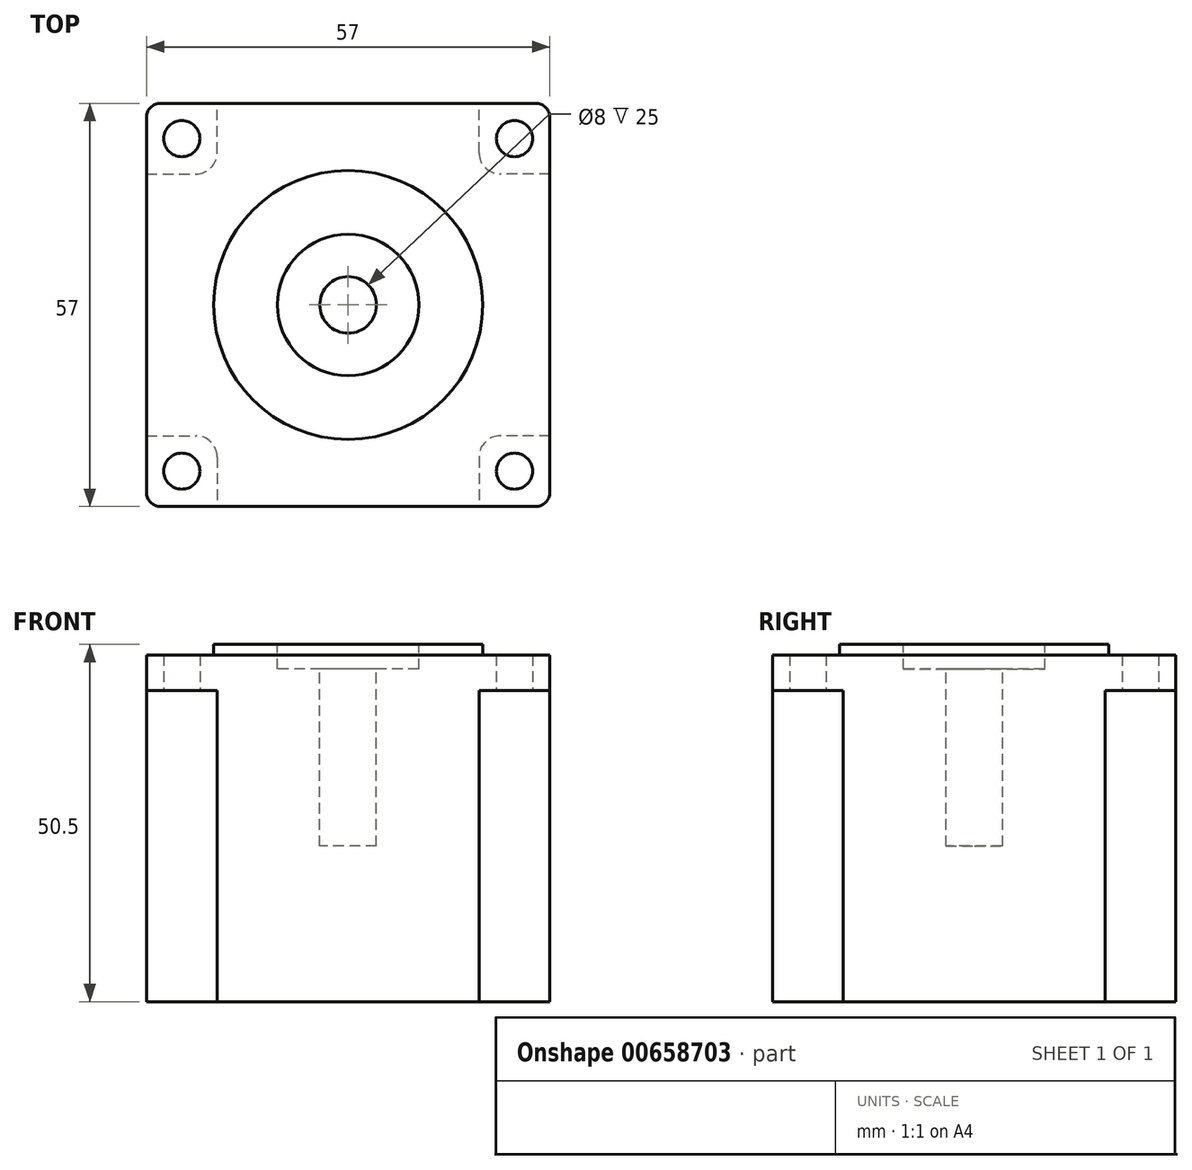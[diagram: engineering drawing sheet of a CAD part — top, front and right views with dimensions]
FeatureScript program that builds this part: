
annotation { "Feature Type Name" : "Feature", "Feature Type Description" : "" }
export const myFeature = defineFeature(function(context is Context, id is Id, definition is map)
    precondition{}
    {
        {
            var Q0;
            Q0=qCreatedBy(makeId("Top.planeOp"),FACE);
            var sketch = newSketch(context, id + "F0", { "sketchPlane" : qUnion([Q0])});
            skLineSegment(sketch, "E0.bottom", {"start": v(-28.5, 28.5) * mm, "end": v(28.5, 28.5) * mm});
            skLineSegment(sketch, "E0.top", {"start": v(-28.5, -28.5) * mm, "end": v(28.5, -28.5) * mm});
            skLineSegment(sketch, "E0.left", {"start": v(-28.5, 28.5) * mm, "end": v(-28.5, -28.5) * mm});
            skLineSegment(sketch, "E0.right", {"start": v(28.5, 28.5) * mm, "end": v(28.5, -28.5) * mm});
            skSolve(sketch);
        }
        {
            var Q0;
            Q0=makeQuery(id+"F0.imprint","IMPRINT",FACE,{"disambiguationData":[TD([[makeQuery(id+"F0.imprint","IMPRINT",EDGE,{"derivedFrom":sQuery(id+"F0.wireOp",EDGE,"E0.bottom")}),-1.0]])]});
            extrude(context, id + "F1", {"entities" : qUnion([Q0]), "depth" : 49 * mm});
        }
        {
            var Q0;
            Q0=makeQuery(id+"F1.opExtrude","SWEPT_EDGE",EDGE,{"disambiguationData":[OSD([sQuery(id+"F0.wireOp",EDGE,"E0.top"),sQuery(id+"F0.wireOp",EDGE,"E0.left")])]});
            var Q1;
            Q1=makeQuery(id+"F1.opExtrude","SWEPT_EDGE",EDGE,{"disambiguationData":[OSD([sQuery(id+"F0.wireOp",EDGE,"E0.top"),sQuery(id+"F0.wireOp",EDGE,"E0.right")])]});
            var Q2;
            Q2=makeQuery(id+"F1.opExtrude","SWEPT_EDGE",EDGE,{"disambiguationData":[OSD([sQuery(id+"F0.wireOp",EDGE,"E0.bottom"),sQuery(id+"F0.wireOp",EDGE,"E0.right")])]});
            var Q3;
            Q3=makeQuery(id+"F1.opExtrude","SWEPT_EDGE",EDGE,{"disambiguationData":[OSD([sQuery(id+"F0.wireOp",EDGE,"E0.bottom"),sQuery(id+"F0.wireOp",EDGE,"E0.left")])]});
            fillet(context, id + "F2", {"entities" : qUnion([Q0, Q1, Q2, Q3]), "radius" : 2 * mm, "tangentPropagation" : true, "allowEdgeOverflow" : false});
        }
        {
            var Q0;
            Q0=makeQuery(id+"F1.opExtrude","CAP_FACE",FACE,{"disambiguationData":[OSD([sQuery(id+"F0.wireOp",EDGE,"E0.bottom"),sQuery(id+"F0.wireOp",EDGE,"E0.top"),sQuery(id+"F0.wireOp",EDGE,"E0.left"),sQuery(id+"F0.wireOp",EDGE,"E0.right")])],"isStart":true});
            var sketch = newSketch(context, id + "F3", { "sketchPlane" : qUnion([Q0])});
            skCircle(sketch, "E1", {"center": v(-23.5, 23.5) * mm, "radius": 2.55 * mm});
            skCircle(sketch, "E2", {"center": v(-23.5, -23.5) * mm, "radius": 2.55 * mm});
            skCircle(sketch, "E3", {"center": v(23.5, -23.5) * mm, "radius": 2.55 * mm});
            skCircle(sketch, "E4", {"center": v(23.5, 23.5) * mm, "radius": 2.55 * mm});
            skSolve(sketch);
        }
        {
            var Q0;
            Q0=makeQuery(id+"F3.imprint","IMPRINT",FACE,{"disambiguationData":[TD([[makeQuery(id+"F3.imprint","IMPRINT",EDGE,{"derivedFrom":sQuery(id+"F3.wireOp",EDGE,"E2")}),1.0]])]});
            var Q1;
            Q1=makeQuery(id+"F3.imprint","IMPRINT",FACE,{"disambiguationData":[TD([[makeQuery(id+"F3.imprint","IMPRINT",EDGE,{"derivedFrom":sQuery(id+"F3.wireOp",EDGE,"E1")}),1.0]])]});
            var Q2;
            Q2=makeQuery(id+"F3.imprint","IMPRINT",FACE,{"disambiguationData":[TD([[makeQuery(id+"F3.imprint","IMPRINT",EDGE,{"derivedFrom":sQuery(id+"F3.wireOp",EDGE,"E4")}),1.0]])]});
            var Q3;
            Q3=makeQuery(id+"F3.imprint","IMPRINT",FACE,{"disambiguationData":[TD([[makeQuery(id+"F3.imprint","IMPRINT",EDGE,{"derivedFrom":sQuery(id+"F3.wireOp",EDGE,"E3")}),1.0]])]});
            extrude(context, id + "F4", {"entities" : qUnion([Q0, Q1, Q2, Q3]), "operationType" : NewBodyOperationType.REMOVE, "endBound" : BoundingType.THROUGH_ALL, "oppositeDirection" : true, "depth" : 25 * mm});
        }
        {
            var Q0;
            Q0=makeQuery(id+"F1.opExtrude","CAP_FACE",FACE,{"disambiguationData":[OSD([sQuery(id+"F0.wireOp",EDGE,"E0.bottom"),sQuery(id+"F0.wireOp",EDGE,"E0.top"),sQuery(id+"F0.wireOp",EDGE,"E0.left"),sQuery(id+"F0.wireOp",EDGE,"E0.right")])],"isStart":true});
            var sketch = newSketch(context, id + "F5", { "sketchPlane" : qUnion([Q0])});
            skLineSegment(sketch, "E5.rect.bottom", {"start": v(28.5, 18.5) * mm, "end": v(18.5, 18.5) * mm});
            skLineSegment(sketch, "E5.rect.top", {"start": v(28.5, 28.5) * mm, "end": v(18.5, 28.5) * mm});
            skLineSegment(sketch, "E5.rect.left", {"start": v(28.5, 18.5) * mm, "end": v(28.5, 28.5) * mm});
            skLineSegment(sketch, "E5.rect.right", {"start": v(18.5, 18.5) * mm, "end": v(18.5, 28.5) * mm});
            skPoint(sketch, "E5.rect.middle", {"position": v(23.5, 23.5) * mm});
            skLineSegment(sketch, "E6.rect.bottom", {"start": v(28.5, -18.5) * mm, "end": v(18.5, -18.5) * mm});
            skLineSegment(sketch, "E6.rect.top", {"start": v(28.5, -28.5) * mm, "end": v(18.5, -28.5) * mm});
            skLineSegment(sketch, "E6.rect.left", {"start": v(28.5, -18.5) * mm, "end": v(28.5, -28.5) * mm});
            skLineSegment(sketch, "E6.rect.right", {"start": v(18.5, -18.5) * mm, "end": v(18.5, -28.5) * mm});
            skPoint(sketch, "E6.rect.middle", {"position": v(23.5, -23.5) * mm});
            skLineSegment(sketch, "E7.rect.bottom", {"start": v(-28.5, -18.5) * mm, "end": v(-18.5, -18.5) * mm});
            skLineSegment(sketch, "E7.rect.top", {"start": v(-28.5, -28.5) * mm, "end": v(-18.5, -28.5) * mm});
            skLineSegment(sketch, "E7.rect.left", {"start": v(-28.5, -18.5) * mm, "end": v(-28.5, -28.5) * mm});
            skLineSegment(sketch, "E7.rect.right", {"start": v(-18.5, -18.5) * mm, "end": v(-18.5, -28.5) * mm});
            skPoint(sketch, "E7.rect.middle", {"position": v(-23.5, -23.5) * mm});
            skLineSegment(sketch, "E8.rect.bottom", {"start": v(-28.5, 18.5) * mm, "end": v(-18.5, 18.5) * mm});
            skLineSegment(sketch, "E8.rect.top", {"start": v(-28.5, 28.5) * mm, "end": v(-18.5, 28.5) * mm});
            skLineSegment(sketch, "E8.rect.left", {"start": v(-28.5, 18.5) * mm, "end": v(-28.5, 28.5) * mm});
            skLineSegment(sketch, "E8.rect.right", {"start": v(-18.5, 18.5) * mm, "end": v(-18.5, 28.5) * mm});
            skPoint(sketch, "E8.rect.middle", {"position": v(-23.5, 23.5) * mm});
            skSolve(sketch);
        }
        {
            var Q0;
            {var subQ5=sQuery(id+"F5.wireOp",EDGE,"E7.rect.bottom");Q0=makeQuery(id+"F5.imprint","IMPRINT",FACE,{"disambiguationData":[TD([[makeQuery(id+"F5.imprint","IMPRINT",EDGE,{"derivedFrom":subQ5}),-1.0]])]});}
            var Q1;
            {var subQ5=sQuery(id+"F5.wireOp",EDGE,"E6.rect.bottom");Q1=makeQuery(id+"F5.imprint","IMPRINT",FACE,{"disambiguationData":[TD([[makeQuery(id+"F5.imprint","IMPRINT",EDGE,{"derivedFrom":subQ5}),1.0]])]});}
            var Q2;
            {var subQ3=sQuery(id+"F5.wireOp",EDGE,"E5.rect.bottom");Q2=makeQuery(id+"F5.imprint","IMPRINT",FACE,{"disambiguationData":[TD([[makeQuery(id+"F5.imprint","IMPRINT",EDGE,{"derivedFrom":subQ3}),-1.0]])]});}
            var Q3;
            {var subQ5=sQuery(id+"F5.wireOp",EDGE,"E8.rect.bottom");Q3=makeQuery(id+"F5.imprint","IMPRINT",FACE,{"disambiguationData":[TD([[makeQuery(id+"F5.imprint","IMPRINT",EDGE,{"derivedFrom":subQ5}),1.0]])]});}
            extrude(context, id + "F6", {"entities" : qUnion([Q0, Q1, Q2, Q3]), "operationType" : NewBodyOperationType.REMOVE, "oppositeDirection" : true, "depth" : 44 * mm});
        }
        {
            var Q0;
            Q0=makeQuery(id+"F6.boolean.opBoolean","COPY",EDGE,{"derivedFrom":makeQuery(id+"F6.opExtrude","SWEPT_EDGE",EDGE,{"disambiguationData":[OSD([sQuery(id+"F5.wireOp",EDGE,"E8.rect.bottom"),sQuery(id+"F5.wireOp",EDGE,"E8.rect.right")])]})});
            var Q1;
            Q1=makeQuery(id+"F6.boolean.opBoolean","COPY",EDGE,{"derivedFrom":makeQuery(id+"F6.opExtrude","SWEPT_EDGE",EDGE,{"disambiguationData":[OSD([sQuery(id+"F0.wireOp",EDGE,"E0.top"),sQuery(id+"F5.wireOp",EDGE,"E8.rect.top"),sQuery(id+"F5.wireOp",EDGE,"E8.rect.right")])]})});
            var Q2;
            Q2=makeQuery(id+"F6.boolean.opBoolean","COPY",EDGE,{"derivedFrom":makeQuery(id+"F6.opExtrude","SWEPT_EDGE",EDGE,{"disambiguationData":[OSD([sQuery(id+"F0.wireOp",EDGE,"E0.left"),sQuery(id+"F5.wireOp",EDGE,"E8.rect.bottom"),sQuery(id+"F5.wireOp",EDGE,"E8.rect.left")])]})});
            var Q3;
            Q3=makeQuery(id+"F6.boolean.opBoolean","COPY",EDGE,{"derivedFrom":makeQuery(id+"F6.opExtrude","SWEPT_EDGE",EDGE,{"disambiguationData":[OSD([sQuery(id+"F0.wireOp",EDGE,"E0.left"),sQuery(id+"F5.wireOp",EDGE,"E7.rect.bottom"),sQuery(id+"F5.wireOp",EDGE,"E7.rect.left")])]})});
            var Q4;
            Q4=makeQuery(id+"F6.boolean.opBoolean","COPY",EDGE,{"derivedFrom":makeQuery(id+"F6.opExtrude","SWEPT_EDGE",EDGE,{"disambiguationData":[OSD([sQuery(id+"F0.wireOp",EDGE,"E0.bottom"),sQuery(id+"F5.wireOp",EDGE,"E7.rect.top"),sQuery(id+"F5.wireOp",EDGE,"E7.rect.right")])]})});
            var Q5;
            Q5=makeQuery(id+"F6.boolean.opBoolean","COPY",EDGE,{"derivedFrom":makeQuery(id+"F6.opExtrude","SWEPT_EDGE",EDGE,{"disambiguationData":[OSD([sQuery(id+"F0.wireOp",EDGE,"E0.top"),sQuery(id+"F5.wireOp",EDGE,"E5.rect.top"),sQuery(id+"F5.wireOp",EDGE,"E5.rect.right")])]})});
            var Q6;
            Q6=makeQuery(id+"F6.boolean.opBoolean","COPY",EDGE,{"derivedFrom":makeQuery(id+"F6.opExtrude","SWEPT_EDGE",EDGE,{"disambiguationData":[OSD([sQuery(id+"F0.wireOp",EDGE,"E0.right"),sQuery(id+"F5.wireOp",EDGE,"E5.rect.bottom"),sQuery(id+"F5.wireOp",EDGE,"E5.rect.left")])]})});
            var Q7;
            Q7=makeQuery(id+"F6.boolean.opBoolean","COPY",EDGE,{"derivedFrom":makeQuery(id+"F6.opExtrude","SWEPT_EDGE",EDGE,{"disambiguationData":[OSD([sQuery(id+"F5.wireOp",EDGE,"E7.rect.bottom"),sQuery(id+"F5.wireOp",EDGE,"E7.rect.right")])]})});
            var Q8;
            Q8=makeQuery(id+"F6.boolean.opBoolean","COPY",EDGE,{"derivedFrom":makeQuery(id+"F6.opExtrude","SWEPT_EDGE",EDGE,{"disambiguationData":[OSD([sQuery(id+"F0.wireOp",EDGE,"E0.right"),sQuery(id+"F5.wireOp",EDGE,"E6.rect.bottom"),sQuery(id+"F5.wireOp",EDGE,"E6.rect.left")])]})});
            var Q9;
            Q9=makeQuery(id+"F6.boolean.opBoolean","COPY",EDGE,{"derivedFrom":makeQuery(id+"F6.opExtrude","SWEPT_EDGE",EDGE,{"disambiguationData":[OSD([sQuery(id+"F0.wireOp",EDGE,"E0.bottom"),sQuery(id+"F5.wireOp",EDGE,"E6.rect.top"),sQuery(id+"F5.wireOp",EDGE,"E6.rect.right")])]})});
            var Q10;
            Q10=makeQuery(id+"F6.boolean.opBoolean","COPY",EDGE,{"derivedFrom":makeQuery(id+"F6.opExtrude","SWEPT_EDGE",EDGE,{"disambiguationData":[OSD([sQuery(id+"F5.wireOp",EDGE,"E6.rect.bottom"),sQuery(id+"F5.wireOp",EDGE,"E6.rect.right")])]})});
            var Q11;
            Q11=makeQuery(id+"F6.boolean.opBoolean","COPY",EDGE,{"derivedFrom":makeQuery(id+"F6.opExtrude","SWEPT_EDGE",EDGE,{"disambiguationData":[OSD([sQuery(id+"F5.wireOp",EDGE,"E5.rect.bottom"),sQuery(id+"F5.wireOp",EDGE,"E5.rect.right")])]})});
            fillet(context, id + "F7", {"entities" : qUnion([Q0, Q1, Q2, Q3, Q4, Q5, Q6, Q7, Q8, Q9, Q10, Q11]), "radius" : 3 * mm, "tangentPropagation" : true, "allowEdgeOverflow" : false});
        }
        {
            var Q0;
            Q0=makeQuery(id+"F1.opExtrude","CAP_FACE",FACE,{"disambiguationData":[OSD([sQuery(id+"F0.wireOp",EDGE,"E0.bottom"),sQuery(id+"F0.wireOp",EDGE,"E0.top"),sQuery(id+"F0.wireOp",EDGE,"E0.left"),sQuery(id+"F0.wireOp",EDGE,"E0.right")])],"isStart":false});
            var sketch = newSketch(context, id + "F8", { "sketchPlane" : qUnion([Q0])});
            skCircle(sketch, "E9", {"center": v(0, 0) * mm, "radius": 10 * mm});
            skSolve(sketch);
        }
        {
            var Q0;
            Q0=makeQuery(id+"F8.imprint","IMPRINT",FACE,{"disambiguationData":[TD([[makeQuery(id+"F8.imprint","IMPRINT",EDGE,{"derivedFrom":sQuery(id+"F8.wireOp",EDGE,"E9")}),1.0]])]});
            extrude(context, id + "F9", {"entities" : qUnion([Q0]), "operationType" : NewBodyOperationType.REMOVE, "oppositeDirection" : true, "depth" : 2 * mm});
        }
        {
            var Q0;
            Q0=makeQuery(id+"F9.boolean.opBoolean","COPY",FACE,{"derivedFrom":makeQuery(id+"F9.opExtrude","CAP_FACE",FACE,{"disambiguationData":[OSD([sQuery(id+"F8.wireOp",EDGE,"E9")])],"isStart":false})});
            var sketch = newSketch(context, id + "F10", { "sketchPlane" : qUnion([Q0])});
            skCircle(sketch, "E10", {"center": v(0, 0) * mm, "radius": 4 * mm});
            skSolve(sketch);
        }
        {
            var Q0;
            Q0=makeQuery(id+"F10.imprint","IMPRINT",FACE,{"disambiguationData":[TD([[makeQuery(id+"F10.imprint","IMPRINT",EDGE,{"derivedFrom":sQuery(id+"F10.wireOp",EDGE,"E10")}),1.0]])]});
            extrude(context, id + "F11", {"entities" : qUnion([Q0]), "operationType" : NewBodyOperationType.REMOVE, "oppositeDirection" : true, "depth" : 25 * mm});
        }
        {
            var Q0;
            Q0=makeQuery(id+"F1.opExtrude","CAP_FACE",FACE,{"disambiguationData":[OSD([sQuery(id+"F0.wireOp",EDGE,"E0.bottom"),sQuery(id+"F0.wireOp",EDGE,"E0.top"),sQuery(id+"F0.wireOp",EDGE,"E0.left"),sQuery(id+"F0.wireOp",EDGE,"E0.right")])],"isStart":false});
            var sketch = newSketch(context, id + "F12", { "sketchPlane" : qUnion([Q0])});
            skCircle(sketch, "E11", {"center": v(0, 0) * mm, "radius": 19 * mm});
            skSolve(sketch);
        }
        {
            var Q0;
            Q0=makeQuery(id+"F12.imprint","IMPRINT",FACE,{"disambiguationData":[TD([[makeQuery(id+"F12.imprint","IMPRINT",EDGE,{"derivedFrom":sQuery(id+"F12.wireOp",EDGE,"E11")}),1.0]])]});
            extrude(context, id + "F13", {"entities" : qUnion([Q0]), "operationType" : NewBodyOperationType.ADD, "depth" : 1.5 * mm});
        }
    });
